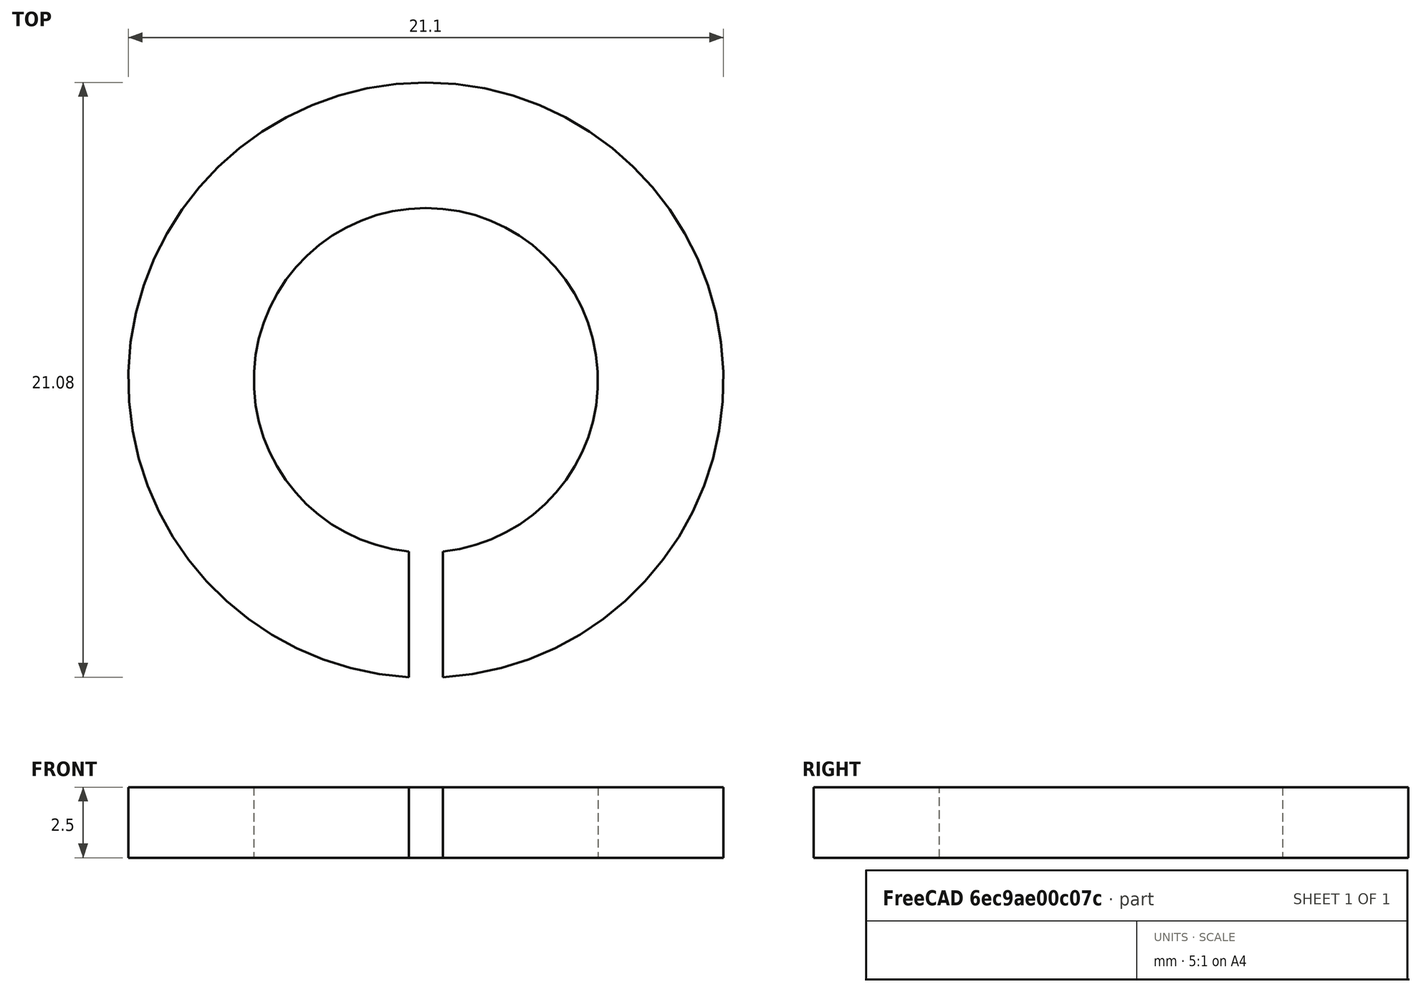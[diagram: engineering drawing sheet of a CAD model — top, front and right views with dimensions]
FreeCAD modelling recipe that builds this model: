
FCSTD DOCUMENT  (FreeCAD 0.15R4651 (Git))
Label: Federring_DIN127-B12
License: All rights reserved
LicenseURL: http://de.wikipedia.org/wiki/Alle_Rechte_vorbehalten
objects: Sketcher::SketchObject×1, PartDesign::Pad×1
note: 3 computed .brp shape members not serialized (recipe doc carries the construction recipe); baked Part::Feature solids carry a one-line shape summary decoded from their .brp

FEATURE [Sketcher::SketchObject] Sketch
  sketch-geometry (4):
    g0: ArcOfCircle CenterX=0 CenterY=0 CenterZ=0 NormalX=0 NormalY=0 NormalZ=1 Radius=6.1 StartAngle=4.81091 EndAngle=10.8971
    g1: ArcOfCircle CenterX=0 CenterY=0 CenterZ=0 NormalX=0 NormalY=0 NormalZ=1 Radius=10.55 StartAngle=4.76929 EndAngle=10.9387
    g2: LineSegment StartX=0.6 StartY=-6.07042 StartZ=0 EndX=0.6 EndY=-10.5329 EndZ=0
    g3: LineSegment StartX=-0.6 StartY=-10.5329 StartZ=0 EndX=-0.6 EndY=-6.07042 EndZ=0
  constraints (12):
    c: Coincident(g0,g-1)
    c: Coincident(g1,g-1)
    c: Vertical(g2)
    c: Vertical(g3)
    c: Coincident(g0,g2)
    c: Coincident(g0,g3)
    c: Coincident(g1,g2)
    c: Coincident(g1,g3)
    c: Symmetric(g1,g1,g-2)
    c: Radius(g0) = 6.1
    c: Radius(g1) = 10.55
    c: DistanceX(g1,g1) = -1.2
FEATURE [PartDesign::Pad] Pad  label="Federring DIN 127-B 12 #"
  Length = 2.5
  Length2 = 100
  Midplane = true
  Sketch = -> Sketch
  Type = 0
